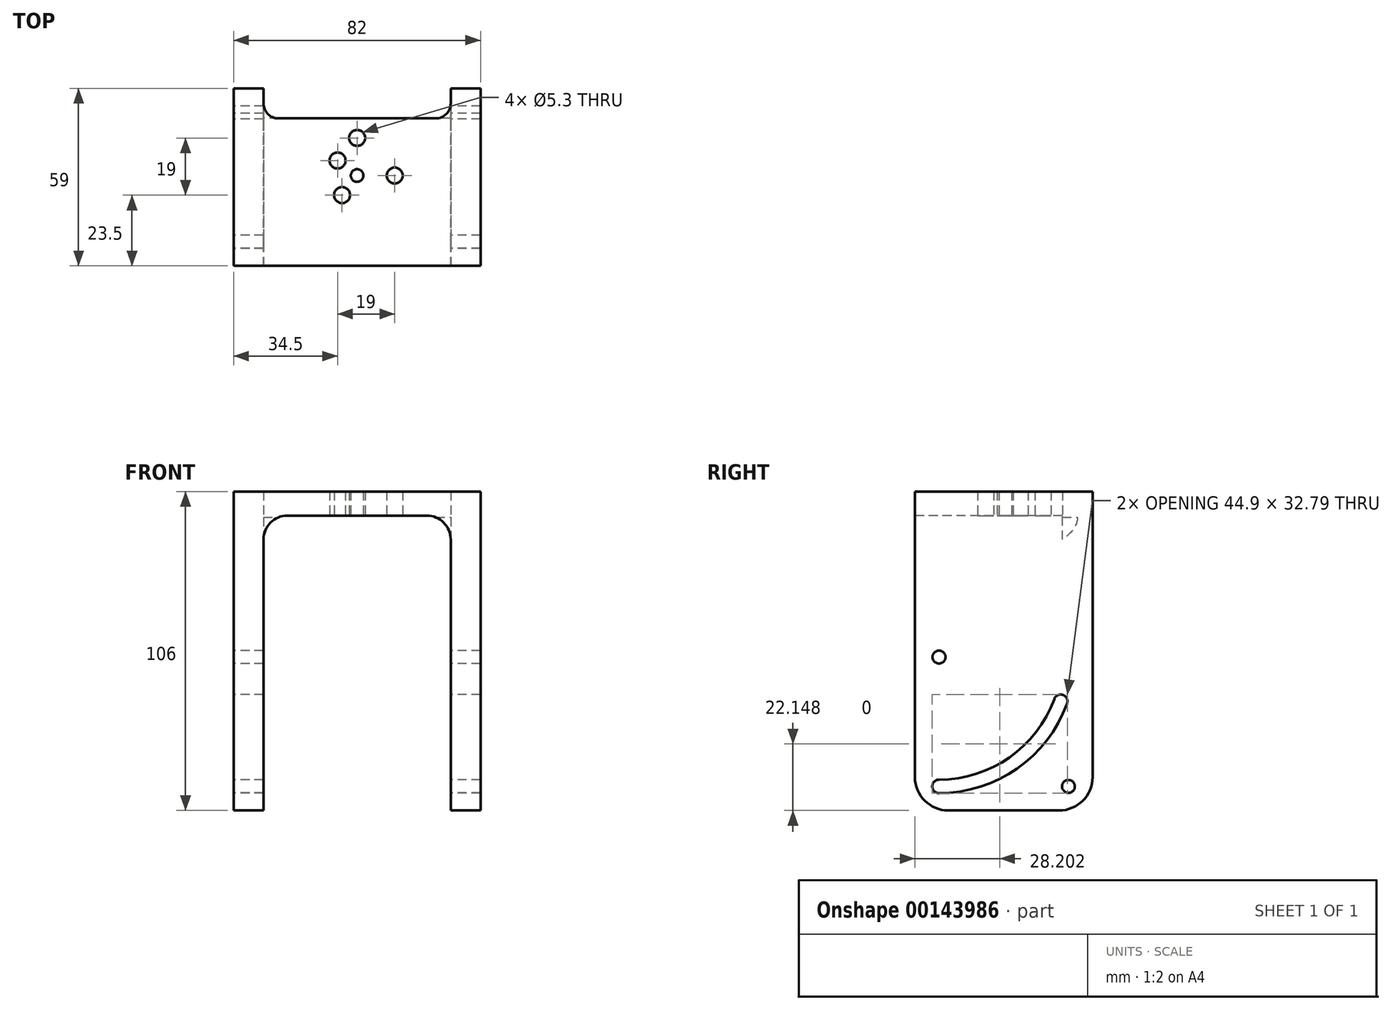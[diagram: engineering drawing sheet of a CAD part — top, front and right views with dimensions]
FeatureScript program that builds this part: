
annotation { "Feature Type Name" : "Feature", "Feature Type Description" : "" }
export const myFeature = defineFeature(function(context is Context, id is Id, definition is map)
    precondition{}
    {
        {
            var Q0;
            Q0=qCreatedBy(makeId("Right.planeOp"),FACE);
            var sketch = newSketch(context, id + "F0", { "sketchPlane" : qUnion([Q0])});
            skCircle(sketch, "E0", {"center": v(0, -31.54) * mm, "radius": 2.25 * mm});
            skCircle(sketch, "E1", {"center": v(0, 11.46) * mm, "radius": 2.15 * mm});
            skCircle(sketch, "E2", {"center": v(40.4, -3.24) * mm, "radius": 2.25 * mm});
            skLineSegment(sketch, "E3", {"start": v(0, 11.46) * mm, "end": v(0, -31.54) * mm});
            skLineSegment(sketch, "E4", {"start": v(0, 11.46) * mm, "end": v(40.4, -3.24) * mm});
            skCircle(sketch, "E5", {"center": v(43, -31.54) * mm, "radius": 2.15 * mm});
            skArc(sketch, "E6", {"start": v(0, -29.29) * mm, "mid": v(23.37, -21.92) * mm, "end": v(38.3, -2.47) * mm});
            skArc(sketch, "E7", {"start": v(0, -33.79) * mm, "mid": v(25.95, -25.6) * mm, "end": v(42.52, -4.01) * mm});
            skLineSegment(sketch, "E8.bottom", {"start": v(-8, 58.46) * mm, "end": v(51, 58.46) * mm});
            skLineSegment(sketch, "E8.top", {"start": v(-8, -39.54) * mm, "end": v(51, -39.54) * mm});
            skLineSegment(sketch, "E8.left", {"start": v(-8, 58.46) * mm, "end": v(-8, -39.54) * mm});
            skLineSegment(sketch, "E8.right", {"start": v(51, 58.46) * mm, "end": v(51, -39.54) * mm});
            skLineSegment(sketch, "E9.top", {"start": v(-8, 66.46) * mm, "end": v(51, 66.46) * mm});
            skLineSegment(sketch, "E9.left", {"start": v(-8, 58.46) * mm, "end": v(-8, 66.46) * mm});
            skLineSegment(sketch, "E9.right", {"start": v(51, 58.46) * mm, "end": v(51, 66.46) * mm});
            skSolve(sketch);
        }
        {
            var Q0;
            Q0=makeQuery(id+"F0.imprint","IMPRINT",FACE,{"disambiguationData":[TD([[makeQuery(id+"F0.imprint","IMPRINT",EDGE,{"derivedFrom":sQuery(id+"F0.wireOp",EDGE,"E8.bottom")}),1.0]])]});
            var Q1;
            Q1=makeQuery(id+"F0.imprint","IMPRINT",FACE,{"disambiguationData":[TD([[makeQuery(id+"F0.imprint","IMPRINT",EDGE,{"derivedFrom":sQuery(id+"F0.wireOp",EDGE,"E5")}),-1.0]])]});
            var Q2;
            {var subQ5=sQuery(id+"F0.wireOp",EDGE,"E6");Q2=makeQuery(id+"F0.imprint","IMPRINT",FACE,{"disambiguationData":[TD([[makeQuery(id+"F0.imprint","IMPRINT",EDGE,{"derivedFrom":subQ5}),1.0]])]});}
            extrude(context, id + "F1", {"entities" : qUnion([Q0, Q1, Q2]), "depth" : 82 * mm, "offsetDistance" : 25 * mm});
        }
        {
            var Q0;
            Q0=makeQuery(id+"F1.opExtrude","SWEPT_FACE",FACE,{"disambiguationData":[OSD([sQuery(id+"F0.wireOp",EDGE,"E8.left"),sQuery(id+"F0.wireOp",EDGE,"E9.left")])]});
            var sketch = newSketch(context, id + "F2", { "sketchPlane" : qUnion([Q0])});
            skLineSegment(sketch, "E10.bottom", {"start": v(9.9, -39.54) * mm, "end": v(72.1, -39.54) * mm});
            skLineSegment(sketch, "E10.top", {"start": v(9.9, 58.46) * mm, "end": v(72.1, 58.46) * mm});
            skLineSegment(sketch, "E10.left", {"start": v(9.9, -39.54) * mm, "end": v(9.9, 58.46) * mm});
            skLineSegment(sketch, "E10.right", {"start": v(72.1, -39.54) * mm, "end": v(72.1, 58.46) * mm});
            skSolve(sketch);
        }
        {
            var Q0;
            Q0=makeQuery(id+"F2.imprint","IMPRINT",FACE,{"disambiguationData":[TD([[makeQuery(id+"F2.imprint","IMPRINT",EDGE,{"derivedFrom":sQuery(id+"F2.wireOp",EDGE,"E10.bottom")}),-1.0]])]});
            extrude(context, id + "F3", {"entities" : qUnion([Q0]), "operationType" : NewBodyOperationType.ADD, "depth" : 25 * mm, "offsetDistance" : 25 * mm});
        }
        {
            var Q0;
            Q0=makeQuery(id+"F3.opExtrude","CAP_FACE",FACE,{"disambiguationData":[OSD([sQuery(id+"F2.wireOp",EDGE,"E10.bottom"),sQuery(id+"F2.wireOp",EDGE,"E10.top"),sQuery(id+"F2.wireOp",EDGE,"E10.left"),sQuery(id+"F2.wireOp",EDGE,"E10.right")])],"isStart":false});
            extrude(context, id + "F4", {"entities" : qUnion([Q0]), "operationType" : NewBodyOperationType.REMOVE, "oppositeDirection" : true, "depth" : 125.3 * mm, "offsetDistance" : 25 * mm});
        }
        {
            var Q0;
            Q0=makeQuery(id+"F4.boolean.opBoolean","COPY",FACE,{"derivedFrom":makeQuery(id+"F4.opExtrude","SWEPT_FACE",FACE,{"disambiguationData":[OSD([sQuery(id+"F2.wireOp",EDGE,"E10.top")])]})});
            var sketch = newSketch(context, id + "F5", { "sketchPlane" : qUnion([Q0])});
            skLineSegment(sketch, "E11", {"start": v(41, 8) * mm, "end": v(41, -51) * mm, "construction": true});
            skCircle(sketch, "E12", {"center": v(41, -22) * mm, "radius": 2.1 * mm});
            skCircle(sketch, "E13", {"center": v(53.5, -22) * mm, "radius": 2.65 * mm});
            skCircle(sketch, "E14", {"center": v(34.5, -27) * mm, "radius": 2.65 * mm});
            skCircle(sketch, "E15.1.0", {"center": v(36, -15.5) * mm, "radius": 2.65 * mm});
            skCircle(sketch, "E15.1.1", {"center": v(41, -34.5) * mm, "radius": 2.65 * mm});
            skLineSegment(sketch, "E15.anchor1", {"start": v(41, -22) * mm, "end": v(34.5, -27) * mm, "construction": true});
            skLineSegment(sketch, "E15.anchor2", {"start": v(41, -22) * mm, "end": v(36, -15.5) * mm, "construction": true});
            skLineSegment(sketch, "E16.bottom", {"start": v(72.1, -51) * mm, "end": v(9.9, -51) * mm});
            skLineSegment(sketch, "E16.top", {"start": v(72.1, -41) * mm, "end": v(9.9, -41) * mm});
            skLineSegment(sketch, "E16.left", {"start": v(72.1, -51) * mm, "end": v(72.1, -41) * mm});
            skLineSegment(sketch, "E16.right", {"start": v(9.9, -51) * mm, "end": v(9.9, -41) * mm});
            skPoint(sketch, "E16.middle", {"position": v(41, -46) * mm});
            skSolve(sketch);
        }
        {
            var Q0;
            {var subQ0=sQuery(id+"F5.wireOp",EDGE,"E12");var subQ1=sQuery(id+"F5.wireOp",EDGE,"E11");var subQ2=makeQuery(id+"F5.imprint","INTERSECT",VERTEX,{"disambiguationData":[OD(0.0)],"derivedFrom":[subQ1,subQ0]});Q0=makeQuery(id+"F5.imprint","IMPRINT",FACE,{"disambiguationData":[TD([[makeQuery(id+"F5.imprint","IMPRINT",EDGE,{"disambiguationData":[TD([[subQ2,-1.0]])],"derivedFrom":subQ1}),-1.0]])]});}
            var Q1;
            {var subQ0=sQuery(id+"F5.wireOp",EDGE,"E12");var subQ1=sQuery(id+"F5.wireOp",EDGE,"E11");var subQ2=makeQuery(id+"F5.imprint","INTERSECT",VERTEX,{"disambiguationData":[OD(0.0)],"derivedFrom":[subQ1,subQ0]});Q1=makeQuery(id+"F5.imprint","IMPRINT",FACE,{"disambiguationData":[TD([[makeQuery(id+"F5.imprint","IMPRINT",EDGE,{"disambiguationData":[TD([[subQ2,-1.0]])],"derivedFrom":subQ1}),1.0]])]});}
            var Q2;
            Q2=makeQuery(id+"F5.imprint","IMPRINT",FACE,{"disambiguationData":[TD([[makeQuery(id+"F5.imprint","IMPRINT",EDGE,{"derivedFrom":sQuery(id+"F5.wireOp",EDGE,"E14")}),1.0]])]});
            var Q3;
            Q3=makeQuery(id+"F5.imprint","IMPRINT",FACE,{"disambiguationData":[TD([[makeQuery(id+"F5.imprint","IMPRINT",EDGE,{"derivedFrom":sQuery(id+"F5.wireOp",EDGE,"E13")}),1.0]])]});
            var Q4;
            Q4=makeQuery(id+"F5.imprint","IMPRINT",FACE,{"disambiguationData":[TD([[makeQuery(id+"F5.imprint","IMPRINT",EDGE,{"derivedFrom":sQuery(id+"F5.wireOp",EDGE,"E15.1.0")}),1.0]])]});
            var Q5;
            Q5=makeQuery(id+"F5.imprint","IMPRINT",FACE,{"disambiguationData":[TD([[makeQuery(id+"F5.imprint","IMPRINT",EDGE,{"derivedFrom":sQuery(id+"F5.wireOp",EDGE,"E12")}),1.0]])]});
            var Q6;
            Q6=makeQuery(id+"F5.imprint","IMPRINT",FACE,{"disambiguationData":[TD([[makeQuery(id+"F5.imprint","IMPRINT",EDGE,{"derivedFrom":sQuery(id+"F5.wireOp",EDGE,"E15.1.1")}),1.0]])]});
            var Q7;
            Q7=makeQuery(id+"F5.imprint","IMPRINT",FACE,{"disambiguationData":[TD([[makeQuery(id+"F5.imprint","IMPRINT",EDGE,{"derivedFrom":sQuery(id+"F5.wireOp",EDGE,"E16.bottom")}),1.0]])]});
            extrude(context, id + "F6", {"entities" : qUnion([Q0, Q1, Q2, Q3, Q4, Q5, Q6, Q7]), "operationType" : NewBodyOperationType.REMOVE, "oppositeDirection" : true, "depth" : 20.8 * mm, "offsetDistance" : 25 * mm});
        }
        {
            var Q0;
            Q0=makeQuery(id+"F4.boolean.opBoolean","COPY",EDGE,{"derivedFrom":makeQuery(id+"F4.opExtrude","SWEPT_EDGE",EDGE,{"disambiguationData":[OSD([sQuery(id+"F2.wireOp",EDGE,"E10.top"),sQuery(id+"F2.wireOp",EDGE,"E10.left")])]})});
            var Q1;
            Q1=makeQuery(id+"F4.boolean.opBoolean","COPY",EDGE,{"derivedFrom":makeQuery(id+"F4.opExtrude","SWEPT_EDGE",EDGE,{"disambiguationData":[OSD([sQuery(id+"F2.wireOp",EDGE,"E10.top"),sQuery(id+"F2.wireOp",EDGE,"E10.right")])]})});
            fillet(context, id + "F7", {"entities" : qUnion([Q0, Q1]), "radius" : 7.97 * mm, "tangentPropagation" : true, "allowEdgeOverflow" : false});
        }
        {
            var Q0;
            {var subQ1=sQuery(id+"F0.wireOp",EDGE,"E8.left");var subQ2=sQuery(id+"F0.wireOp",EDGE,"E8.top");Q0=makeQuery(id+"F3.boolean.opBoolean","SPLIT",EDGE,{"disambiguationData":[TD([makeQuery(id+"F3.opExtrude","SWEPT_FACE",FACE,{"disambiguationData":[OSD([sQuery(id+"F2.wireOp",EDGE,"E10.left")])]})])],"derivedFrom":makeQuery(id+"F1.opExtrude","SWEPT_EDGE",EDGE,{"disambiguationData":[OSD([subQ2,subQ1])]})});}
            var Q1;
            {var subQ1=sQuery(id+"F0.wireOp",EDGE,"E8.right");var subQ2=sQuery(id+"F0.wireOp",EDGE,"E8.top");Q1=makeQuery(id+"F4.boolean.opBoolean","SPLIT",EDGE,{"disambiguationData":[TD([makeQuery(id+"F4.opExtrude","SWEPT_FACE",FACE,{"disambiguationData":[OSD([sQuery(id+"F2.wireOp",EDGE,"E10.left")])]})])],"derivedFrom":makeQuery(id+"F1.opExtrude","SWEPT_EDGE",EDGE,{"disambiguationData":[OSD([subQ2,subQ1])]})});}
            var Q2;
            {var subQ1=sQuery(id+"F0.wireOp",EDGE,"E8.right");var subQ2=sQuery(id+"F0.wireOp",EDGE,"E8.top");Q2=makeQuery(id+"F4.boolean.opBoolean","SPLIT",EDGE,{"disambiguationData":[TD([makeQuery(id+"F4.opExtrude","SWEPT_FACE",FACE,{"disambiguationData":[OSD([sQuery(id+"F2.wireOp",EDGE,"E10.right")])]})])],"derivedFrom":makeQuery(id+"F1.opExtrude","SWEPT_EDGE",EDGE,{"disambiguationData":[OSD([subQ2,subQ1])]})});}
            var Q3;
            {var subQ1=sQuery(id+"F0.wireOp",EDGE,"E8.left");var subQ2=sQuery(id+"F0.wireOp",EDGE,"E8.top");Q3=makeQuery(id+"F3.boolean.opBoolean","SPLIT",EDGE,{"disambiguationData":[TD([makeQuery(id+"F3.opExtrude","SWEPT_FACE",FACE,{"disambiguationData":[OSD([sQuery(id+"F2.wireOp",EDGE,"E10.right")])]})])],"derivedFrom":makeQuery(id+"F1.opExtrude","SWEPT_EDGE",EDGE,{"disambiguationData":[OSD([subQ2,subQ1])]})});}
            fillet(context, id + "F8", {"entities" : qUnion([Q0, Q1, Q2, Q3]), "radius" : 11.1 * mm, "tangentPropagation" : true, "allowEdgeOverflow" : false});
        }
        {
            var Q0;
            Q0=makeQuery(id+"F6.boolean.opBoolean","COPY",EDGE,{"derivedFrom":makeQuery(id+"F6.opExtrude","SWEPT_EDGE",EDGE,{"disambiguationData":[OSD([sQuery(id+"F2.wireOp",EDGE,"E10.top"),sQuery(id+"F2.wireOp",EDGE,"E10.left"),sQuery(id+"F5.wireOp",EDGE,"E16.top"),sQuery(id+"F5.wireOp",EDGE,"E16.right")])]})});
            var Q1;
            Q1=makeQuery(id+"F6.boolean.opBoolean","COPY",EDGE,{"derivedFrom":makeQuery(id+"F6.opExtrude","SWEPT_EDGE",EDGE,{"disambiguationData":[OSD([sQuery(id+"F2.wireOp",EDGE,"E10.top"),sQuery(id+"F2.wireOp",EDGE,"E10.right"),sQuery(id+"F5.wireOp",EDGE,"E16.top"),sQuery(id+"F5.wireOp",EDGE,"E16.left")])]})});
            fillet(context, id + "F9", {"entities" : qUnion([Q0, Q1]), "radius" : 5 * mm, "tangentPropagation" : true, "allowEdgeOverflow" : false});
        }
    });
